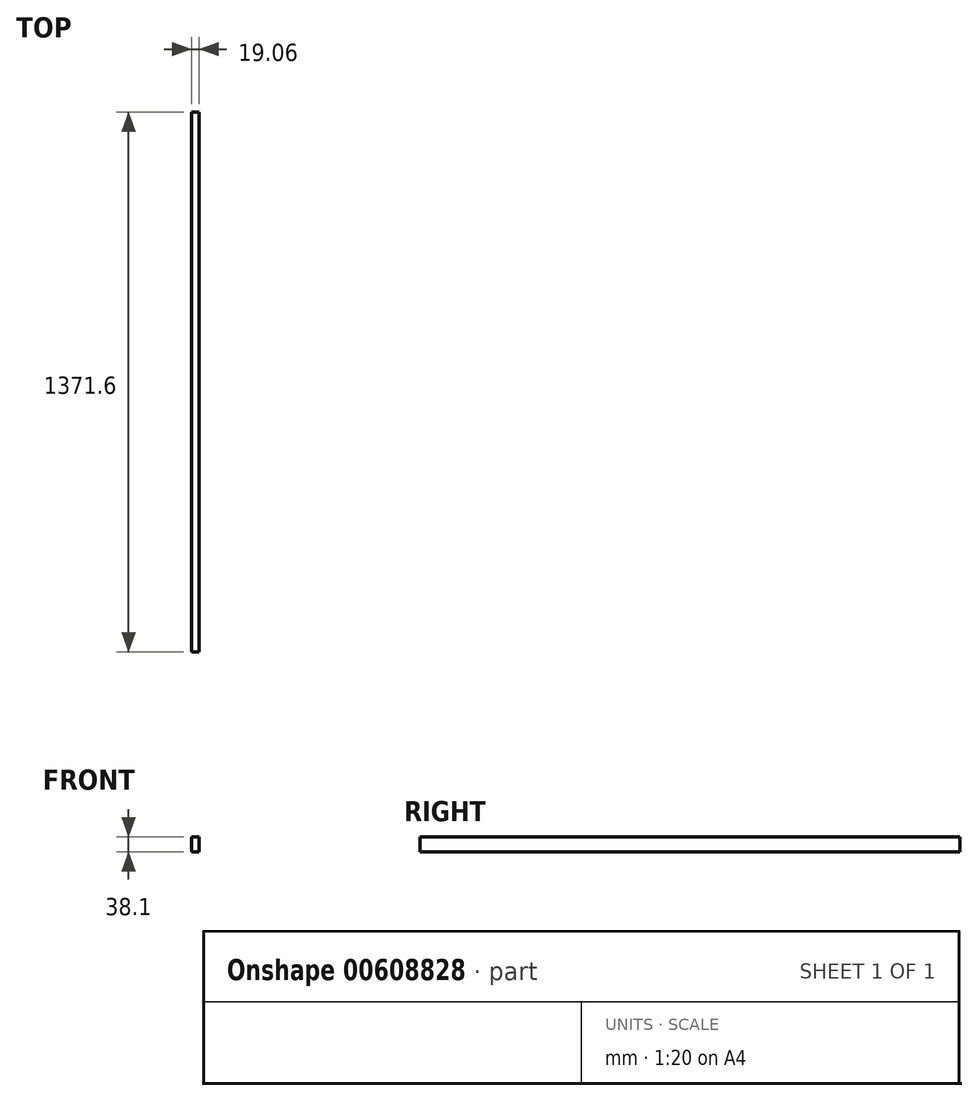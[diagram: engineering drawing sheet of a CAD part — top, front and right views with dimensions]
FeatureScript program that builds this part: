
annotation { "Feature Type Name" : "Feature", "Feature Type Description" : "" }
export const myFeature = defineFeature(function(context is Context, id is Id, definition is map)
    precondition{}
    {
        {
            var Q0;
            Q0=qCreatedBy(makeId("Front.planeOp"),FACE);
            var sketch = newSketch(context, id + "F0", { "sketchPlane" : qUnion([Q0])});
            skLineSegment(sketch, "E0.bottom", {"start": v(9.52, 19.05) * mm, "end": v(-9.53, 19.05) * mm});
            skLineSegment(sketch, "E0.top", {"start": v(9.53, -19.05) * mm, "end": v(-9.52, -19.05) * mm});
            skLineSegment(sketch, "E0.left", {"start": v(9.52, 19.05) * mm, "end": v(9.53, -19.05) * mm});
            skLineSegment(sketch, "E0.right", {"start": v(-9.53, 19.05) * mm, "end": v(-9.52, -19.05) * mm});
            skPoint(sketch, "E0.middle", {"position": v(0, 0) * mm});
            skSolve(sketch);
        }
        {
            var Q0;
            Q0=qSketchRegion(id+"F0",true);
            extrude(context, id + "F1", {"entities" : qUnion([Q0]), "endBound" : BoundingType.SYMMETRIC, "depth" : 1371.6 * mm, "offsetDistance" : 25.4 * mm});
        }
    });
